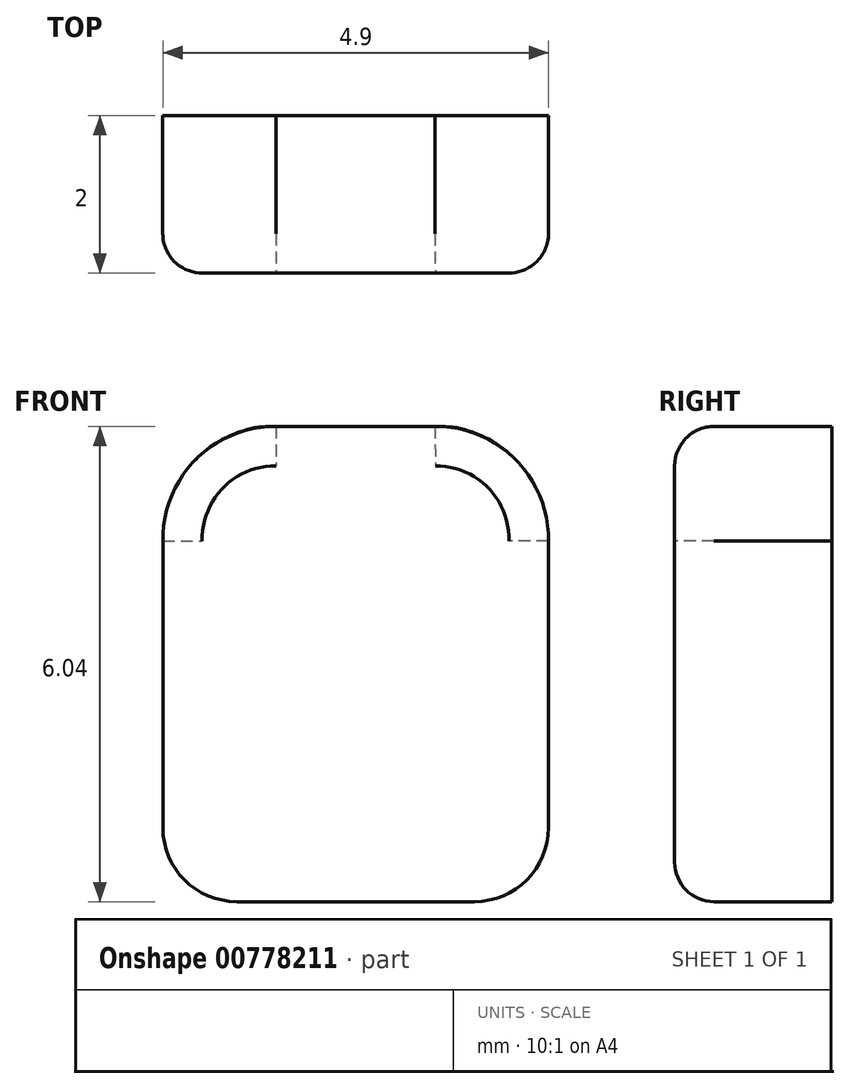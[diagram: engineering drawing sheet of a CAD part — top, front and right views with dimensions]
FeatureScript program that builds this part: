
annotation { "Feature Type Name" : "Feature", "Feature Type Description" : "" }
export const myFeature = defineFeature(function(context is Context, id is Id, definition is map)
    precondition{}
    {
        {
            var Q0;
            Q0=qCreatedBy(makeId("Front.planeOp"),FACE);
            var sketch = newSketch(context, id + "F0", { "sketchPlane" : qUnion([Q0])});
            skFitSpline(sketch, "E0.0", {"points": [v(2.52, 1.58) * mm, v(2.52, 1.68) * mm, v(2.5, 1.87) * mm, v(2.42, 2.14) * mm, v(2.28, 2.4) * mm, v(2.1, 2.62) * mm, v(1.89, 2.8) * mm, v(1.64, 2.94) * mm, v(1.36, 3.02) * mm, v(1.17, 3.04) * mm, v(1.08, 3.04) * mm]});
            skLineSegment(sketch, "E0.1", {"start": v(2.52, -2.06) * mm, "end": v(2.52, 1.58) * mm});
            skLineSegment(sketch, "E0.2", {"start": v(1.08, 3.04) * mm, "end": v(-0.94, 3.04) * mm});
            skArc(sketch, "E0.3", {"start": v(1.58, -3) * mm, "mid": v(2.24, -2.72) * mm, "end": v(2.52, -2.06) * mm});
            skFitSpline(sketch, "E0.4", {"points": [v(-0.94, 3.04) * mm, v(-1.04, 3.04) * mm, v(-1.22, 3.02) * mm, v(-1.5, 2.94) * mm, v(-1.75, 2.8) * mm, v(-1.97, 2.62) * mm, v(-2.15, 2.4) * mm, v(-2.28, 2.14) * mm, v(-2.36, 1.87) * mm, v(-2.38, 1.68) * mm, v(-2.38, 1.58) * mm]});
            skLineSegment(sketch, "E0.5", {"start": v(-2.38, 1.58) * mm, "end": v(-2.38, -2.06) * mm});
            skArc(sketch, "E0.6", {"start": v(-2.38, -2.06) * mm, "mid": v(-2.1, -2.72) * mm, "end": v(-1.44, -3) * mm});
            skLineSegment(sketch, "E0.7", {"start": v(-1.44, -3) * mm, "end": v(1.58, -3) * mm});
            skSolve(sketch);
        }
        {
            var Q0;
            Q0=makeQuery(id+"F0.imprint","IMPRINT",FACE,{"disambiguationData":[TD([[makeQuery(id+"F0.imprint","IMPRINT",EDGE,{"derivedFrom":sQuery(id+"F0.wireOp",EDGE,"E0.0")}),1.0]])]});
            extrude(context, id + "F1", {"entities" : qUnion([Q0]), "depth" : 2 * mm, "offsetDistance" : 25 * mm});
        }
        {
            var Q0;
            Q0=makeQuery(id+"F1.opExtrude","CAP_EDGE",EDGE,{"disambiguationData":[OSD([sQuery(id+"F0.wireOp",EDGE,"E0.5")])],"isStart":false});
            fillet(context, id + "F2", {"entities" : qUnion([Q0]), "radius" : .5 * mm, "tangentPropagation" : true, "allowEdgeOverflow" : false});
        }
    });
